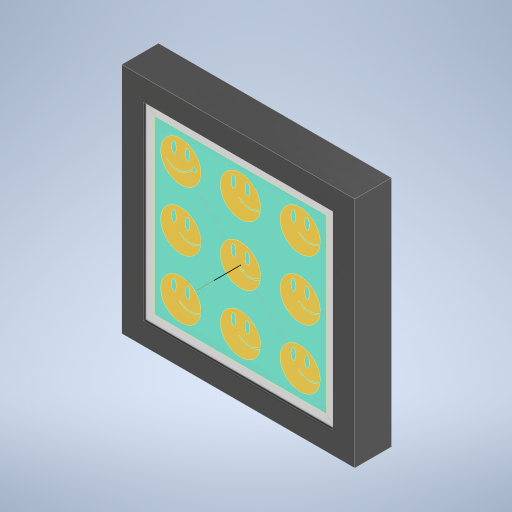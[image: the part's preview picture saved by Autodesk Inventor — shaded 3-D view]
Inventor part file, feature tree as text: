
AUTODESK INVENTOR PART (.ipt)
format: ipt  version: 2023 (Build 270158030, 158C)  size: 722,944 bytes
history: native  units: mm
features: sketch x14, extrude x13, projected_geometry x9, other x7, pattern_circular x1
ambient origin geometry x8: Origin, YZ Plane, XZ Plane, XY Plane, X Axis, Y Axis, Z Axis, Center Point
bodies: Body1 (feature_tree), Body2 (feature_tree), Body3 (feature_tree), Body4 (feature_tree), Body5 (feature_tree)
feature tree (44):
  other  "art"
  extrude  "Extrusion1"  Depth=185.0mm
  extrude  "Extrusion2"  Depth=0.02mm TaperAngle=0.0deg
  extrude  "Extrusion3"  Depth=23.0mm
  extrude  "Extrusion4"  Depth=5.0mm
  extrude  "Extrusion6"  Depth=5.0mm
  extrude  "Extrusion10"  Depth=6.0mm
  extrude  "Extrusion11"  Depth=8.0mm
  extrude  "Extrusion12"  Depth=0.02mm TaperAngle=0.0deg
  extrude  "Extrusion13"  Depth=1.5mm
  sketch  "Sketch21"  dims[d40=25.0mm d41=0.0mm]
  other  "Work Axis1"
  pattern_circular  "Circular Pattern2"  Count=15  [1 undecoded]
  extrude  "Extrusion14"  Depth=17.5mm
  extrude  "Extrusion15"  Depth=17.5mm
  extrude  "Extrusion16"  Depth=200.0mm
  extrude  "Extrusion17"  Depth=200.0mm
  sketch  "Sketch1"  dims[d0=175.0mm d1=185.0mm]
  sketch  "Sketch2"  dims[d2=0.01mm d3=0.0mm d8=0.02mm d9=0.0mm]
  sketch  "Sketch3"  dims[d10=35.0mm d11=23.0mm]
  sketch  "Sketch4"  dims[d12=23.0mm d13=5.0mm]
  other  "back-plate"
  sketch  "Sketch7"  dims[d14=5.0mm d15=2.0mm]
  projected_geometry  "Projected Loop9"
  sketch  "Sketch13"  dims[d16=2.0mm d17=6.0mm]
  projected_geometry  "Projected Loop17"
  sketch  "Sketch15"  dims[d18=6.0mm d19=8.0mm]
  projected_geometry  "Projected Loop18"
  sketch  "Sketch16"  dims[d20=30.0mm d22=52.0mm d23=30.0mm d25=52.0mm d28=0.02mm d29=0.0mm]
  sketch  "Sketch18"  dims[d34=2.0mm d35=0.0mm d39=1.5mm]
  projected_geometry  "Projected Loop19"
  other  "Pattern of back-plate:1"
  other  "back-plate-revolve"
  sketch  "Sketch22"  dims[d42=15.0mm d69=150.0mm]
  projected_geometry  "Projected Loop20"
  projected_geometry  "Projected Loop21"
  other  "closure1"
  sketch  "Sketch23"  dims[d70=150.0mm d71=17.5mm]
  projected_geometry  "Projected Loop22"
  sketch  "Sketch24"  dims[d72=17.5mm d73=12.5mm]
  projected_geometry  "Projected Loop23"
  other  "outer"
  sketch  "Sketch25"  dims[d74=12.5mm d76=200.0mm d77=200.0mm d78=7.5mm d79=7.5mm d80=12.5mm d81=12.5mm d82=15.0mm d83=15.0mm d84=200.0mm d85=55.0mm d86=55.0mm d87=15.0mm d88=40.0mm d90=360.0deg d92=3.0mm d93=0.0mm d101=0.0mm d102=0.0mm d103=15.0mm d104=8.0mm d105=5.0mm d106=13.0mm d107=7.5mm d108=7.5mm d109=2.0mm d110=0.0mm d113=15.0mm d114=7.5mm d115=8.0mm d116=13.0mm d117=8.0mm d118=8.0mm d119=7.5mm d120=8.0mm d121=13.0mm d122=2.0mm d123=0.0mm d130=20.0mm d131=360.0deg d133=10.0mm d134=10.0mm d136=10.0mm d139=1.5mm d140=1.5mm d141=1.5mm d142=1.5mm d143=19.0mm d144=19.0mm d145=19.0mm d146=19.0mm d147=2.0mm d148=0.0mm d149=2.0mm d150=0.0mm d151=1.5mm d152=50.0mm d153=0.0mm d154=15.0mm d155=3.0mm d156=0.0mm]
  projected_geometry  "Projected Loop24"
note: 1 required parameter value undecoded (feature->parameter linkage not recoverable at this tier; creation-order binding heuristic only, values carry confidence <= 0.55)
